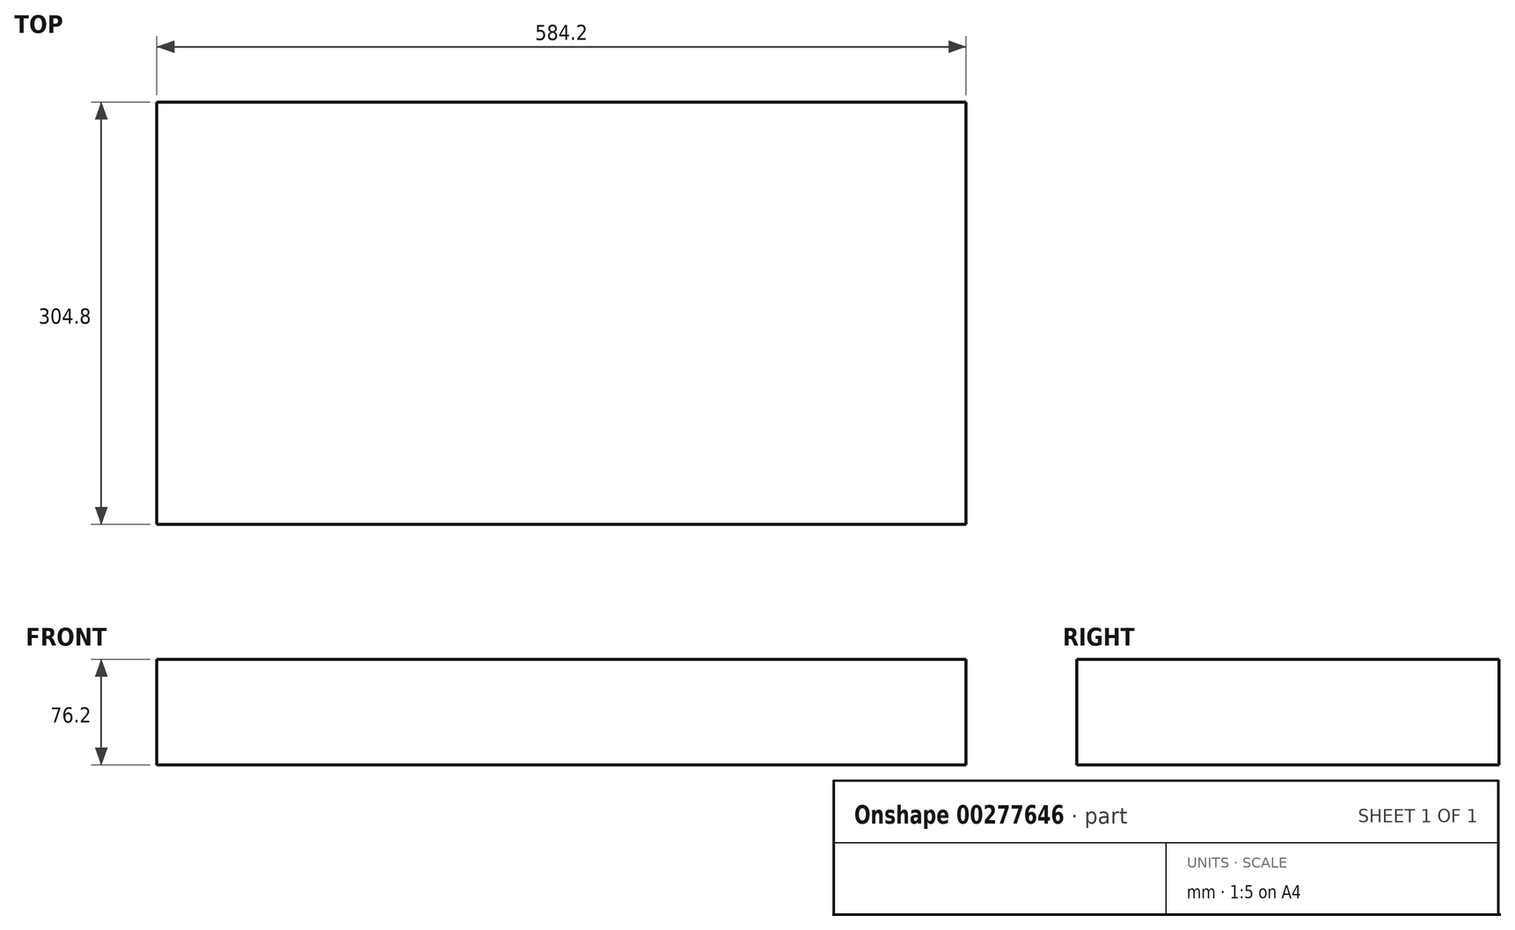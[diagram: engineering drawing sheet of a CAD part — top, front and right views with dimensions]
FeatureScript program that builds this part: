
annotation { "Feature Type Name" : "Feature", "Feature Type Description" : "" }
export const myFeature = defineFeature(function(context is Context, id is Id, definition is map)
    precondition{}
    {
        {
            var Q0;
            Q0=qCreatedBy(makeId("Top.planeOp"),FACE);
            var sketch = newSketch(context, id + "F0", { "sketchPlane" : qUnion([Q0])});
            skLineSegment(sketch, "E0.bottom", {"start": v(292.1, 152.4) * mm, "end": v(-292.1, 152.4) * mm});
            skLineSegment(sketch, "E0.top", {"start": v(292.1, -152.4) * mm, "end": v(-292.1, -152.4) * mm});
            skLineSegment(sketch, "E0.left", {"start": v(292.1, 152.4) * mm, "end": v(292.1, -152.4) * mm});
            skLineSegment(sketch, "E0.right", {"start": v(-292.1, 152.4) * mm, "end": v(-292.1, -152.4) * mm});
            skPoint(sketch, "E0.middle", {"position": v(0, 0) * mm});
            skSolve(sketch);
        }
        {
            var Q0;
            Q0 = qSketchRegion(id + "F0", true);
            extrude(context, id + "F1", {"entities" : qUnion([Q0]), "endBound" : BoundingType.SYMMETRIC, "depth" : 76.2 * mm});
        }
    });
